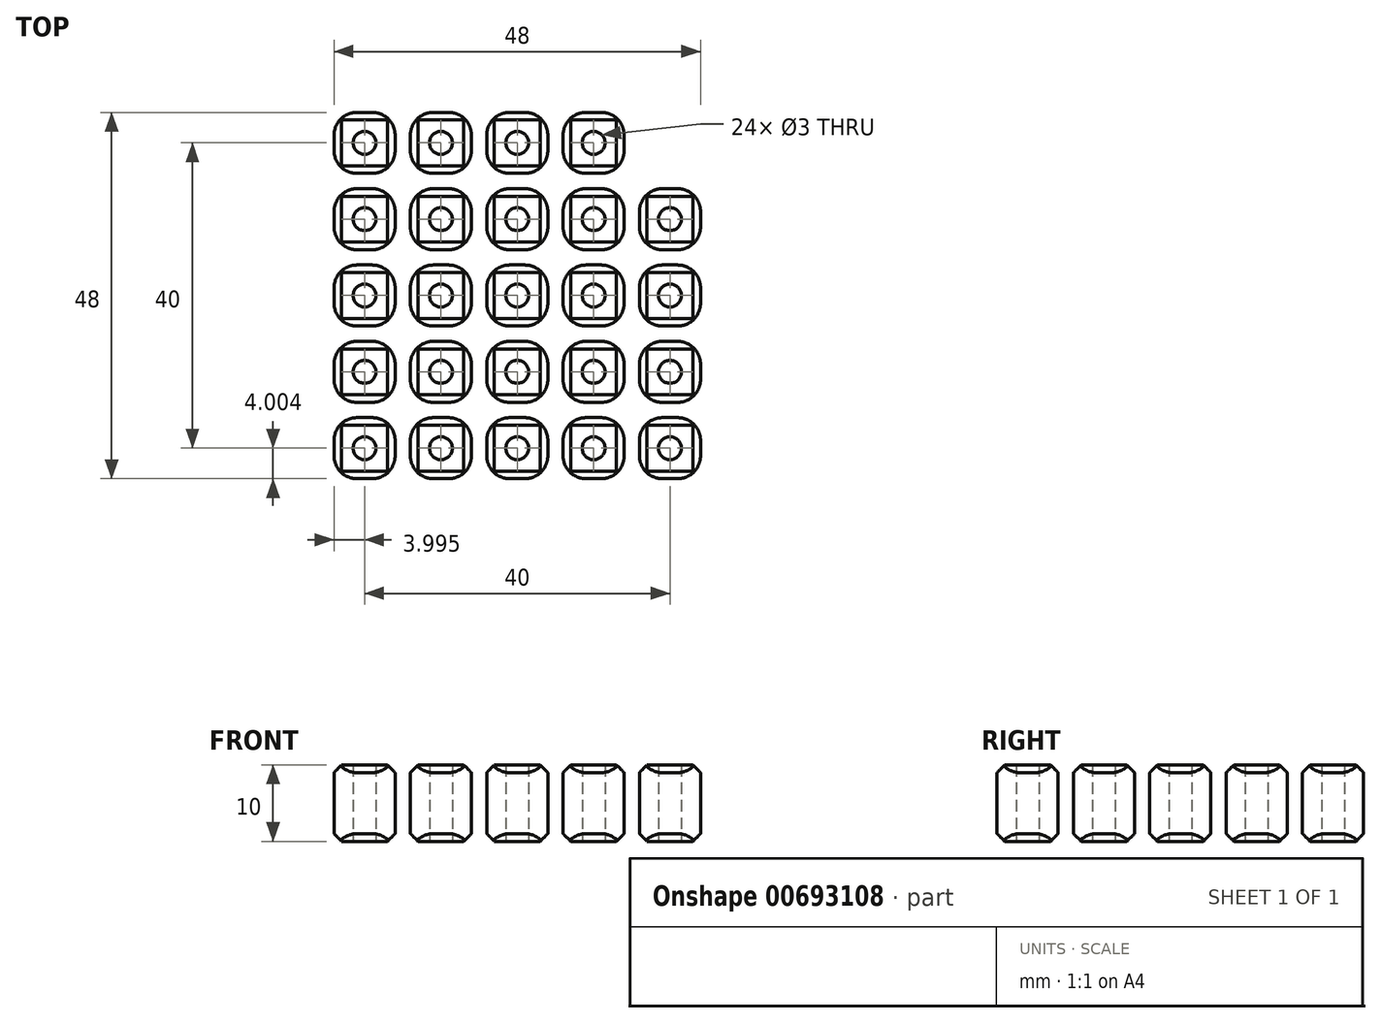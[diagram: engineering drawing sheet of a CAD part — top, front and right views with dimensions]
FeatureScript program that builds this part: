
annotation { "Feature Type Name" : "Feature", "Feature Type Description" : "" }
export const myFeature = defineFeature(function(context is Context, id is Id, definition is map)
    precondition{}
    {
        {
            var Q0;
            Q0=qCreatedBy(makeId("Top.planeOp"),FACE);
            var sketch = newSketch(context, id + "F0", { "sketchPlane" : qUnion([Q0])});
            skLineSegment(sketch, "E0.bottom", {"start": v(-10.33, 9.6) * mm, "end": v(-2.33, 9.6) * mm});
            skLineSegment(sketch, "E0.top", {"start": v(-10.33, 1.6) * mm, "end": v(-2.33, 1.6) * mm});
            skLineSegment(sketch, "E0.left", {"start": v(-10.33, 9.6) * mm, "end": v(-10.33, 1.6) * mm});
            skLineSegment(sketch, "E0.right", {"start": v(-2.33, 9.6) * mm, "end": v(-2.33, 1.6) * mm});
            skSolve(sketch);
        }
        {
            var Q0;
            Q0 = qSketchRegion(id + "F0", true);
            extrude(context, id + "F1", {"entities" : qUnion([Q0]), "depth" : 10 * mm, "offsetDistance" : 25 * mm});
        }
        {
            var Q0;
            Q0=makeQuery(id+"F0.imprint","IMPRINT",FACE,{"disambiguationData":[TD([[makeQuery(id+"F0.imprint","IMPRINT",EDGE,{"derivedFrom":sQuery(id+"F0.wireOp",EDGE,"E0.bottom")}),-1.0]])]});
            var sketch = newSketch(context, id + "F2", { "sketchPlane" : qUnion([Q0])});
            skCircle(sketch, "E1", {"center": v(-6.33, 5.6) * mm, "radius": 1.5 * mm});
            skSolve(sketch);
        }
        {
            var Q0;
            Q0 = qSketchRegion(id + "F2", true);
            extrude(context, id + "F3", {"entities" : qUnion([Q0]), "operationType" : NewBodyOperationType.REMOVE, "depth" : 10 * mm, "offsetDistance" : 25 * mm});
        }
        {
            var Q0;
            Q0=makeQuery(id+"F1.opExtrude","CAP_EDGE",EDGE,{"disambiguationData":[OSD([sQuery(id+"F0.wireOp",EDGE,"E0.right")])],"isStart":true});
            var Q1;
            Q1=makeQuery(id+"F1.opExtrude","CAP_EDGE",EDGE,{"disambiguationData":[OSD([sQuery(id+"F0.wireOp",EDGE,"E0.bottom")])],"isStart":true});
            var Q2;
            Q2=makeQuery(id+"F1.opExtrude","CAP_EDGE",EDGE,{"disambiguationData":[OSD([sQuery(id+"F0.wireOp",EDGE,"E0.left")])],"isStart":true});
            var Q3;
            Q3=makeQuery(id+"F1.opExtrude","CAP_EDGE",EDGE,{"disambiguationData":[OSD([sQuery(id+"F0.wireOp",EDGE,"E0.top")])],"isStart":true});
            var Q4;
            Q4=makeQuery(id+"F1.opExtrude","CAP_EDGE",EDGE,{"disambiguationData":[OSD([sQuery(id+"F0.wireOp",EDGE,"E0.right")])],"isStart":false});
            var Q5;
            Q5=makeQuery(id+"F1.opExtrude","CAP_EDGE",EDGE,{"disambiguationData":[OSD([sQuery(id+"F0.wireOp",EDGE,"E0.bottom")])],"isStart":false});
            var Q6;
            Q6=makeQuery(id+"F1.opExtrude","CAP_EDGE",EDGE,{"disambiguationData":[OSD([sQuery(id+"F0.wireOp",EDGE,"E0.left")])],"isStart":false});
            var Q7;
            Q7=makeQuery(id+"F1.opExtrude","CAP_EDGE",EDGE,{"disambiguationData":[OSD([sQuery(id+"F0.wireOp",EDGE,"E0.top")])],"isStart":false});
            chamfer(context, id + "F4", {"entities" : qUnion([Q0, Q1, Q2, Q3, Q4, Q5, Q6, Q7]), "width" : 1 * mm, "tangentPropagation" : true});
        }
        {
            var Q0;
            Q0=makeQuery(id+"F1.opExtrude","SWEPT_EDGE",EDGE,{"disambiguationData":[OSD([sQuery(id+"F0.wireOp",EDGE,"E0.top"),sQuery(id+"F0.wireOp",EDGE,"E0.left")])]});
            var Q1;
            Q1=makeQuery(id+"F1.opExtrude","SWEPT_EDGE",EDGE,{"disambiguationData":[OSD([sQuery(id+"F0.wireOp",EDGE,"E0.top"),sQuery(id+"F0.wireOp",EDGE,"E0.right")])]});
            var Q2;
            Q2=makeQuery(id+"F1.opExtrude","SWEPT_EDGE",EDGE,{"disambiguationData":[OSD([sQuery(id+"F0.wireOp",EDGE,"E0.bottom"),sQuery(id+"F0.wireOp",EDGE,"E0.left")])]});
            var Q3;
            Q3=makeQuery(id+"F1.opExtrude","SWEPT_EDGE",EDGE,{"disambiguationData":[OSD([sQuery(id+"F0.wireOp",EDGE,"E0.bottom"),sQuery(id+"F0.wireOp",EDGE,"E0.right")])]});
            fillet(context, id + "F5", {"entities" : qUnion([Q0, Q1, Q2, Q3]), "radius" : 3 * mm, "tangentPropagation" : true, "allowEdgeOverflow" : false});
        }
        {
            var Q0;
            Q0=makeQuery(id+"F1.opExtrude","SWEPT_BODY",BODY,{"disambiguationData":[OSD([sQuery(id+"F0.wireOp",EDGE,"E0.bottom"),sQuery(id+"F0.wireOp",EDGE,"E0.top"),sQuery(id+"F0.wireOp",EDGE,"E0.left"),sQuery(id+"F0.wireOp",EDGE,"E0.right")])]});
            transform(context, id + "F6", {"entities" : qUnion([Q0]), "transformType" : TransformType.TRANSLATION_3D, "dx" : 10 * mm, "dy" : 0 * mm, "dz" : 0 * mm, "makeCopy" : true});
        }
        {
            var Q0;
            Q0=makeQuery(id+"F1.opExtrude","SWEPT_BODY",BODY,{"disambiguationData":[OSD([sQuery(id+"F0.wireOp",EDGE,"E0.bottom"),sQuery(id+"F0.wireOp",EDGE,"E0.top"),sQuery(id+"F0.wireOp",EDGE,"E0.left"),sQuery(id+"F0.wireOp",EDGE,"E0.right")])]});
            transform(context, id + "F7", {"entities" : qUnion([Q0]), "transformType" : TransformType.TRANSLATION_3D, "dx" : 20 * mm, "dy" : 0 * mm, "dz" : 0 * mm, "makeCopy" : true});
        }
        {
            var Q0;
            Q0=makeQuery(id+"F1.opExtrude","SWEPT_BODY",BODY,{"disambiguationData":[OSD([sQuery(id+"F0.wireOp",EDGE,"E0.bottom"),sQuery(id+"F0.wireOp",EDGE,"E0.top"),sQuery(id+"F0.wireOp",EDGE,"E0.left"),sQuery(id+"F0.wireOp",EDGE,"E0.right")])]});
            transform(context, id + "F8", {"entities" : qUnion([Q0]), "transformType" : TransformType.TRANSLATION_3D, "dx" : 30 * mm, "dy" : 0 * mm, "dz" : 0 * mm, "makeCopy" : true});
        }
        {
            var Q0;
            Q0=makeQuery(id+"F1.opExtrude","SWEPT_BODY",BODY,{"disambiguationData":[OSD([sQuery(id+"F0.wireOp",EDGE,"E0.bottom"),sQuery(id+"F0.wireOp",EDGE,"E0.top"),sQuery(id+"F0.wireOp",EDGE,"E0.left"),sQuery(id+"F0.wireOp",EDGE,"E0.right")])]});
            transform(context, id + "F9", {"entities" : qUnion([Q0]), "transformType" : TransformType.TRANSLATION_3D, "dx" : 40 * mm, "dy" : 0 * mm, "dz" : 0 * mm, "makeCopy" : true});
        }
        {
            var Q0;
            Q0=makeQuery(id+"F1.opExtrude","SWEPT_BODY",BODY,{"disambiguationData":[OSD([sQuery(id+"F0.wireOp",EDGE,"E0.bottom"),sQuery(id+"F0.wireOp",EDGE,"E0.top"),sQuery(id+"F0.wireOp",EDGE,"E0.left"),sQuery(id+"F0.wireOp",EDGE,"E0.right")])]});
            transform(context, id + "F10", {"entities" : qUnion([Q0]), "transformType" : TransformType.TRANSLATION_3D, "dx" : 0 * mm, "dy" : 10 * mm, "dz" : 0 * mm, "makeCopy" : true});
        }
        {
            var Q0;
            Q0=makeQuery(id+"F10.opPattern","COPY",BODY,{"derivedFrom":makeQuery(id+"F1.opExtrude","SWEPT_BODY",BODY,{"disambiguationData":[OSD([sQuery(id+"F0.wireOp",EDGE,"E0.bottom"),sQuery(id+"F0.wireOp",EDGE,"E0.top"),sQuery(id+"F0.wireOp",EDGE,"E0.left"),sQuery(id+"F0.wireOp",EDGE,"E0.right")])]}),"instanceName":"1"});
            transform(context, id + "F11", {"entities" : qUnion([Q0]), "transformType" : TransformType.TRANSLATION_3D, "dx" : 10 * mm, "dy" : 0 * mm, "dz" : 0 * mm, "makeCopy" : true});
        }
        {
            var Q0;
            Q0=makeQuery(id+"F11.opPattern","COPY",BODY,{"derivedFrom":makeQuery(id+"F10.opPattern","COPY",BODY,{"derivedFrom":makeQuery(id+"F1.opExtrude","SWEPT_BODY",BODY,{"disambiguationData":[OSD([sQuery(id+"F0.wireOp",EDGE,"E0.bottom"),sQuery(id+"F0.wireOp",EDGE,"E0.top"),sQuery(id+"F0.wireOp",EDGE,"E0.left"),sQuery(id+"F0.wireOp",EDGE,"E0.right")])]}),"instanceName":"1"}),"instanceName":"1"});
            transform(context, id + "F12", {"entities" : qUnion([Q0]), "transformType" : TransformType.TRANSLATION_3D, "dx" : 10 * mm, "dy" : 0 * mm, "dz" : 0 * mm, "makeCopy" : true});
        }
        {
            var Q0;
            Q0=makeQuery(id+"F12.opPattern","COPY",BODY,{"derivedFrom":makeQuery(id+"F11.opPattern","COPY",BODY,{"derivedFrom":makeQuery(id+"F10.opPattern","COPY",BODY,{"derivedFrom":makeQuery(id+"F1.opExtrude","SWEPT_BODY",BODY,{"disambiguationData":[OSD([sQuery(id+"F0.wireOp",EDGE,"E0.bottom"),sQuery(id+"F0.wireOp",EDGE,"E0.top"),sQuery(id+"F0.wireOp",EDGE,"E0.left"),sQuery(id+"F0.wireOp",EDGE,"E0.right")])]}),"instanceName":"1"}),"instanceName":"1"}),"instanceName":"1"});
            transform(context, id + "F13", {"entities" : qUnion([Q0]), "transformType" : TransformType.TRANSLATION_3D, "dx" : 19 * mm, "dy" : 0 * mm, "dz" : 0 * mm, "makeCopy" : true});
        }
        {
            var Q0;
            Q0=makeQuery(id+"F13.opPattern","COPY",BODY,{"derivedFrom":makeQuery(id+"F12.opPattern","COPY",BODY,{"derivedFrom":makeQuery(id+"F11.opPattern","COPY",BODY,{"derivedFrom":makeQuery(id+"F10.opPattern","COPY",BODY,{"derivedFrom":makeQuery(id+"F1.opExtrude","SWEPT_BODY",BODY,{"disambiguationData":[OSD([sQuery(id+"F0.wireOp",EDGE,"E0.bottom"),sQuery(id+"F0.wireOp",EDGE,"E0.top"),sQuery(id+"F0.wireOp",EDGE,"E0.left"),sQuery(id+"F0.wireOp",EDGE,"E0.right")])]}),"instanceName":"1"}),"instanceName":"1"}),"instanceName":"1"}),"instanceName":"1"});
            deleteBodies(context, id + "F14", {"entities" : qUnion([Q0])});
        }
        {
            var Q0;
            Q0=makeQuery(id+"F12.opPattern","COPY",BODY,{"derivedFrom":makeQuery(id+"F11.opPattern","COPY",BODY,{"derivedFrom":makeQuery(id+"F10.opPattern","COPY",BODY,{"derivedFrom":makeQuery(id+"F1.opExtrude","SWEPT_BODY",BODY,{"disambiguationData":[OSD([sQuery(id+"F0.wireOp",EDGE,"E0.bottom"),sQuery(id+"F0.wireOp",EDGE,"E0.top"),sQuery(id+"F0.wireOp",EDGE,"E0.left"),sQuery(id+"F0.wireOp",EDGE,"E0.right")])]}),"instanceName":"1"}),"instanceName":"1"}),"instanceName":"1"});
            transform(context, id + "F15", {"entities" : qUnion([Q0]), "transformType" : TransformType.TRANSLATION_3D, "dx" : 10 * mm, "dy" : 0 * mm, "dz" : 0 * mm, "makeCopy" : true});
        }
        {
            var Q0;
            Q0=makeQuery(id+"F15.opPattern","COPY",BODY,{"derivedFrom":makeQuery(id+"F12.opPattern","COPY",BODY,{"derivedFrom":makeQuery(id+"F11.opPattern","COPY",BODY,{"derivedFrom":makeQuery(id+"F10.opPattern","COPY",BODY,{"derivedFrom":makeQuery(id+"F1.opExtrude","SWEPT_BODY",BODY,{"disambiguationData":[OSD([sQuery(id+"F0.wireOp",EDGE,"E0.bottom"),sQuery(id+"F0.wireOp",EDGE,"E0.top"),sQuery(id+"F0.wireOp",EDGE,"E0.left"),sQuery(id+"F0.wireOp",EDGE,"E0.right")])]}),"instanceName":"1"}),"instanceName":"1"}),"instanceName":"1"}),"instanceName":"1"});
            transform(context, id + "F16", {"entities" : qUnion([Q0]), "transformType" : TransformType.TRANSLATION_3D, "dx" : 10 * mm, "dy" : 0 * mm, "dz" : 0 * mm, "makeCopy" : true});
        }
        {
            var Q0;
            Q0=makeQuery(id+"F10.opPattern","COPY",BODY,{"derivedFrom":makeQuery(id+"F1.opExtrude","SWEPT_BODY",BODY,{"disambiguationData":[OSD([sQuery(id+"F0.wireOp",EDGE,"E0.bottom"),sQuery(id+"F0.wireOp",EDGE,"E0.top"),sQuery(id+"F0.wireOp",EDGE,"E0.left"),sQuery(id+"F0.wireOp",EDGE,"E0.right")])]}),"instanceName":"1"});
            transform(context, id + "F17", {"entities" : qUnion([Q0]), "transformType" : TransformType.TRANSLATION_3D, "dx" : 0 * mm, "dy" : 10 * mm, "dz" : 0 * mm, "makeCopy" : true});
        }
        {
            var Q0;
            Q0=makeQuery(id+"F17.opPattern","COPY",BODY,{"derivedFrom":makeQuery(id+"F10.opPattern","COPY",BODY,{"derivedFrom":makeQuery(id+"F1.opExtrude","SWEPT_BODY",BODY,{"disambiguationData":[OSD([sQuery(id+"F0.wireOp",EDGE,"E0.bottom"),sQuery(id+"F0.wireOp",EDGE,"E0.top"),sQuery(id+"F0.wireOp",EDGE,"E0.left"),sQuery(id+"F0.wireOp",EDGE,"E0.right")])]}),"instanceName":"1"}),"instanceName":"1"});
            transform(context, id + "F18", {"entities" : qUnion([Q0]), "transformType" : TransformType.TRANSLATION_3D, "dx" : 10 * mm, "dy" : 0 * mm, "dz" : 0 * mm, "makeCopy" : true});
        }
        {
            var Q0;
            Q0=makeQuery(id+"F18.opPattern","COPY",BODY,{"derivedFrom":makeQuery(id+"F17.opPattern","COPY",BODY,{"derivedFrom":makeQuery(id+"F10.opPattern","COPY",BODY,{"derivedFrom":makeQuery(id+"F1.opExtrude","SWEPT_BODY",BODY,{"disambiguationData":[OSD([sQuery(id+"F0.wireOp",EDGE,"E0.bottom"),sQuery(id+"F0.wireOp",EDGE,"E0.top"),sQuery(id+"F0.wireOp",EDGE,"E0.left"),sQuery(id+"F0.wireOp",EDGE,"E0.right")])]}),"instanceName":"1"}),"instanceName":"1"}),"instanceName":"1"});
            transform(context, id + "F19", {"entities" : qUnion([Q0]), "transformType" : TransformType.TRANSLATION_3D, "dx" : 10 * mm, "dy" : 0 * mm, "dz" : 0 * mm, "makeCopy" : true});
        }
        {
            var Q0;
            Q0=makeQuery(id+"F19.opPattern","COPY",BODY,{"derivedFrom":makeQuery(id+"F18.opPattern","COPY",BODY,{"derivedFrom":makeQuery(id+"F17.opPattern","COPY",BODY,{"derivedFrom":makeQuery(id+"F10.opPattern","COPY",BODY,{"derivedFrom":makeQuery(id+"F1.opExtrude","SWEPT_BODY",BODY,{"disambiguationData":[OSD([sQuery(id+"F0.wireOp",EDGE,"E0.bottom"),sQuery(id+"F0.wireOp",EDGE,"E0.top"),sQuery(id+"F0.wireOp",EDGE,"E0.left"),sQuery(id+"F0.wireOp",EDGE,"E0.right")])]}),"instanceName":"1"}),"instanceName":"1"}),"instanceName":"1"}),"instanceName":"1"});
            transform(context, id + "F20", {"entities" : qUnion([Q0]), "transformType" : TransformType.TRANSLATION_3D, "dx" : 10 * mm, "dy" : 0 * mm, "dz" : 0 * mm, "makeCopy" : true});
        }
        {
            var Q0;
            Q0=makeQuery(id+"F20.opPattern","COPY",BODY,{"derivedFrom":makeQuery(id+"F19.opPattern","COPY",BODY,{"derivedFrom":makeQuery(id+"F18.opPattern","COPY",BODY,{"derivedFrom":makeQuery(id+"F17.opPattern","COPY",BODY,{"derivedFrom":makeQuery(id+"F10.opPattern","COPY",BODY,{"derivedFrom":makeQuery(id+"F1.opExtrude","SWEPT_BODY",BODY,{"disambiguationData":[OSD([sQuery(id+"F0.wireOp",EDGE,"E0.bottom"),sQuery(id+"F0.wireOp",EDGE,"E0.top"),sQuery(id+"F0.wireOp",EDGE,"E0.left"),sQuery(id+"F0.wireOp",EDGE,"E0.right")])]}),"instanceName":"1"}),"instanceName":"1"}),"instanceName":"1"}),"instanceName":"1"}),"instanceName":"1"});
            transform(context, id + "F21", {"entities" : qUnion([Q0]), "transformType" : TransformType.TRANSLATION_3D, "dx" : 10 * mm, "dy" : 0 * mm, "dz" : 0 * mm, "makeCopy" : true});
        }
        {
            var Q0;
            Q0=makeQuery(id+"F17.opPattern","COPY",BODY,{"derivedFrom":makeQuery(id+"F10.opPattern","COPY",BODY,{"derivedFrom":makeQuery(id+"F1.opExtrude","SWEPT_BODY",BODY,{"disambiguationData":[OSD([sQuery(id+"F0.wireOp",EDGE,"E0.bottom"),sQuery(id+"F0.wireOp",EDGE,"E0.top"),sQuery(id+"F0.wireOp",EDGE,"E0.left"),sQuery(id+"F0.wireOp",EDGE,"E0.right")])]}),"instanceName":"1"}),"instanceName":"1"});
            transform(context, id + "F22", {"entities" : qUnion([Q0]), "transformType" : TransformType.TRANSLATION_3D, "dx" : 0 * mm, "dy" : 10 * mm, "dz" : 0 * mm, "makeCopy" : true});
        }
        {
            var Q0;
            Q0=makeQuery(id+"F22.opPattern","COPY",BODY,{"derivedFrom":makeQuery(id+"F17.opPattern","COPY",BODY,{"derivedFrom":makeQuery(id+"F10.opPattern","COPY",BODY,{"derivedFrom":makeQuery(id+"F1.opExtrude","SWEPT_BODY",BODY,{"disambiguationData":[OSD([sQuery(id+"F0.wireOp",EDGE,"E0.bottom"),sQuery(id+"F0.wireOp",EDGE,"E0.top"),sQuery(id+"F0.wireOp",EDGE,"E0.left"),sQuery(id+"F0.wireOp",EDGE,"E0.right")])]}),"instanceName":"1"}),"instanceName":"1"}),"instanceName":"1"});
            transform(context, id + "F23", {"entities" : qUnion([Q0]), "transformType" : TransformType.TRANSLATION_3D, "dx" : 10 * mm, "dy" : 0 * mm, "dz" : 0 * mm, "makeCopy" : true});
        }
        {
            var Q0;
            Q0=makeQuery(id+"F23.opPattern","COPY",BODY,{"derivedFrom":makeQuery(id+"F22.opPattern","COPY",BODY,{"derivedFrom":makeQuery(id+"F17.opPattern","COPY",BODY,{"derivedFrom":makeQuery(id+"F10.opPattern","COPY",BODY,{"derivedFrom":makeQuery(id+"F1.opExtrude","SWEPT_BODY",BODY,{"disambiguationData":[OSD([sQuery(id+"F0.wireOp",EDGE,"E0.bottom"),sQuery(id+"F0.wireOp",EDGE,"E0.top"),sQuery(id+"F0.wireOp",EDGE,"E0.left"),sQuery(id+"F0.wireOp",EDGE,"E0.right")])]}),"instanceName":"1"}),"instanceName":"1"}),"instanceName":"1"}),"instanceName":"1"});
            transform(context, id + "F24", {"entities" : qUnion([Q0]), "transformType" : TransformType.TRANSLATION_3D, "dx" : 10 * mm, "dy" : 0 * mm, "dz" : 0 * mm, "makeCopy" : true});
        }
        {
            var Q0;
            Q0=makeQuery(id+"F24.opPattern","COPY",BODY,{"derivedFrom":makeQuery(id+"F23.opPattern","COPY",BODY,{"derivedFrom":makeQuery(id+"F22.opPattern","COPY",BODY,{"derivedFrom":makeQuery(id+"F17.opPattern","COPY",BODY,{"derivedFrom":makeQuery(id+"F10.opPattern","COPY",BODY,{"derivedFrom":makeQuery(id+"F1.opExtrude","SWEPT_BODY",BODY,{"disambiguationData":[OSD([sQuery(id+"F0.wireOp",EDGE,"E0.bottom"),sQuery(id+"F0.wireOp",EDGE,"E0.top"),sQuery(id+"F0.wireOp",EDGE,"E0.left"),sQuery(id+"F0.wireOp",EDGE,"E0.right")])]}),"instanceName":"1"}),"instanceName":"1"}),"instanceName":"1"}),"instanceName":"1"}),"instanceName":"1"});
            transform(context, id + "F25", {"entities" : qUnion([Q0]), "transformType" : TransformType.TRANSLATION_3D, "dx" : 10 * mm, "dy" : 0 * mm, "dz" : 0 * mm, "makeCopy" : true});
        }
        {
            var Q0;
            Q0=makeQuery(id+"F25.opPattern","COPY",BODY,{"derivedFrom":makeQuery(id+"F24.opPattern","COPY",BODY,{"derivedFrom":makeQuery(id+"F23.opPattern","COPY",BODY,{"derivedFrom":makeQuery(id+"F22.opPattern","COPY",BODY,{"derivedFrom":makeQuery(id+"F17.opPattern","COPY",BODY,{"derivedFrom":makeQuery(id+"F10.opPattern","COPY",BODY,{"derivedFrom":makeQuery(id+"F1.opExtrude","SWEPT_BODY",BODY,{"disambiguationData":[OSD([sQuery(id+"F0.wireOp",EDGE,"E0.bottom"),sQuery(id+"F0.wireOp",EDGE,"E0.top"),sQuery(id+"F0.wireOp",EDGE,"E0.left"),sQuery(id+"F0.wireOp",EDGE,"E0.right")])]}),"instanceName":"1"}),"instanceName":"1"}),"instanceName":"1"}),"instanceName":"1"}),"instanceName":"1"}),"instanceName":"1"});
            transform(context, id + "F26", {"entities" : qUnion([Q0]), "transformType" : TransformType.TRANSLATION_3D, "dx" : 10 * mm, "dy" : 0 * mm, "dz" : 0 * mm, "makeCopy" : true});
        }
        {
            var Q0;
            Q0=makeQuery(id+"F22.opPattern","COPY",BODY,{"derivedFrom":makeQuery(id+"F17.opPattern","COPY",BODY,{"derivedFrom":makeQuery(id+"F10.opPattern","COPY",BODY,{"derivedFrom":makeQuery(id+"F1.opExtrude","SWEPT_BODY",BODY,{"disambiguationData":[OSD([sQuery(id+"F0.wireOp",EDGE,"E0.bottom"),sQuery(id+"F0.wireOp",EDGE,"E0.top"),sQuery(id+"F0.wireOp",EDGE,"E0.left"),sQuery(id+"F0.wireOp",EDGE,"E0.right")])]}),"instanceName":"1"}),"instanceName":"1"}),"instanceName":"1"});
            transform(context, id + "F27", {"entities" : qUnion([Q0]), "transformType" : TransformType.TRANSLATION_3D, "dx" : 0 * mm, "dy" : 10 * mm, "dz" : 0 * mm, "makeCopy" : true});
        }
        {
            var Q0;
            Q0=makeQuery(id+"F27.opPattern","COPY",BODY,{"derivedFrom":makeQuery(id+"F22.opPattern","COPY",BODY,{"derivedFrom":makeQuery(id+"F17.opPattern","COPY",BODY,{"derivedFrom":makeQuery(id+"F10.opPattern","COPY",BODY,{"derivedFrom":makeQuery(id+"F1.opExtrude","SWEPT_BODY",BODY,{"disambiguationData":[OSD([sQuery(id+"F0.wireOp",EDGE,"E0.bottom"),sQuery(id+"F0.wireOp",EDGE,"E0.top"),sQuery(id+"F0.wireOp",EDGE,"E0.left"),sQuery(id+"F0.wireOp",EDGE,"E0.right")])]}),"instanceName":"1"}),"instanceName":"1"}),"instanceName":"1"}),"instanceName":"1"});
            transform(context, id + "F28", {"entities" : qUnion([Q0]), "transformType" : TransformType.TRANSLATION_3D, "dx" : 10 * mm, "dy" : 0 * mm, "dz" : 0 * mm, "makeCopy" : true});
        }
        {
            var Q0;
            Q0=makeQuery(id+"F28.opPattern","COPY",BODY,{"derivedFrom":makeQuery(id+"F27.opPattern","COPY",BODY,{"derivedFrom":makeQuery(id+"F22.opPattern","COPY",BODY,{"derivedFrom":makeQuery(id+"F17.opPattern","COPY",BODY,{"derivedFrom":makeQuery(id+"F10.opPattern","COPY",BODY,{"derivedFrom":makeQuery(id+"F1.opExtrude","SWEPT_BODY",BODY,{"disambiguationData":[OSD([sQuery(id+"F0.wireOp",EDGE,"E0.bottom"),sQuery(id+"F0.wireOp",EDGE,"E0.top"),sQuery(id+"F0.wireOp",EDGE,"E0.left"),sQuery(id+"F0.wireOp",EDGE,"E0.right")])]}),"instanceName":"1"}),"instanceName":"1"}),"instanceName":"1"}),"instanceName":"1"}),"instanceName":"1"});
            transform(context, id + "F29", {"entities" : qUnion([Q0]), "transformType" : TransformType.TRANSLATION_3D, "dx" : 10 * mm, "dy" : 0 * mm, "dz" : 0 * mm, "makeCopy" : true});
        }
        {
            var Q0;
            Q0=makeQuery(id+"F29.opPattern","COPY",BODY,{"derivedFrom":makeQuery(id+"F28.opPattern","COPY",BODY,{"derivedFrom":makeQuery(id+"F27.opPattern","COPY",BODY,{"derivedFrom":makeQuery(id+"F22.opPattern","COPY",BODY,{"derivedFrom":makeQuery(id+"F17.opPattern","COPY",BODY,{"derivedFrom":makeQuery(id+"F10.opPattern","COPY",BODY,{"derivedFrom":makeQuery(id+"F1.opExtrude","SWEPT_BODY",BODY,{"disambiguationData":[OSD([sQuery(id+"F0.wireOp",EDGE,"E0.bottom"),sQuery(id+"F0.wireOp",EDGE,"E0.top"),sQuery(id+"F0.wireOp",EDGE,"E0.left"),sQuery(id+"F0.wireOp",EDGE,"E0.right")])]}),"instanceName":"1"}),"instanceName":"1"}),"instanceName":"1"}),"instanceName":"1"}),"instanceName":"1"}),"instanceName":"1"});
            transform(context, id + "F30", {"entities" : qUnion([Q0]), "transformType" : TransformType.TRANSLATION_3D, "dx" : 10 * mm, "dy" : 0 * mm, "dz" : 0 * mm, "makeCopy" : true});
        }
    });
